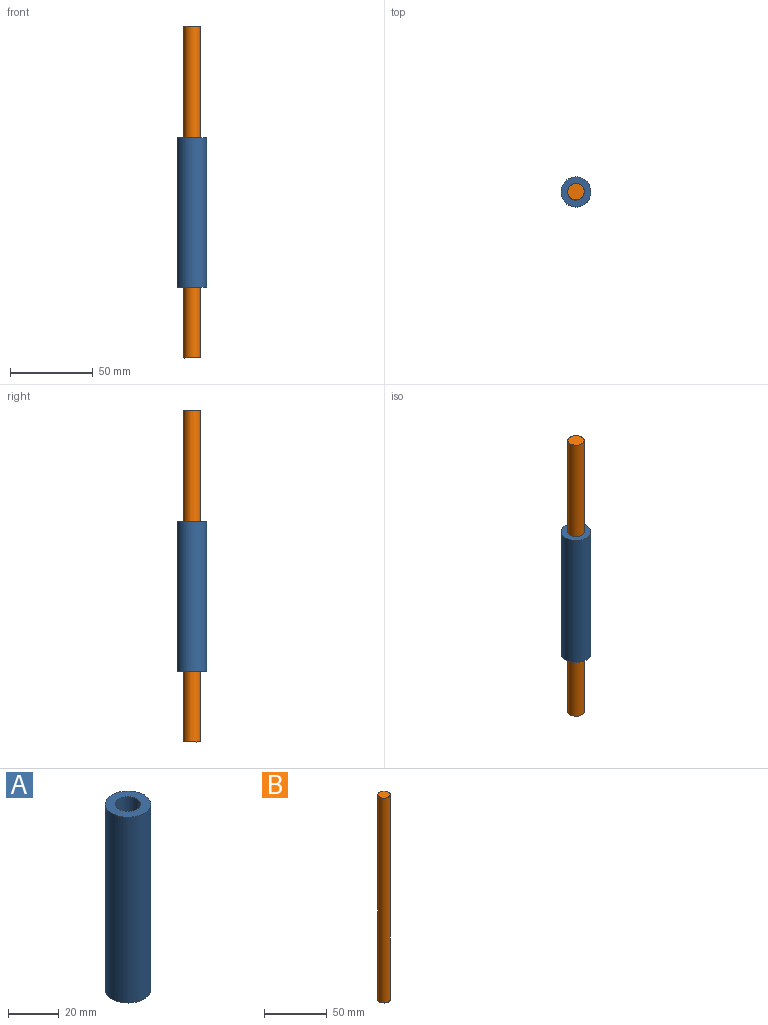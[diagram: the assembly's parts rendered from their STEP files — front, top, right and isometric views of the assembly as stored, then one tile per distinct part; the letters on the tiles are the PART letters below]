
ASSEMBLY  parts=2 mates=1
PART A: 4 faces, bbox 18x18x90 mm
  f0: cylinder r=5mm len=90mm, axis (0,0,-1), area 2827.4mm2, adj f2,f3
  f1: cylinder r=9mm len=90mm, axis (0,0,-1), area 5089.4mm2, adj f2,f3
  f2: plane 18x18mm, normal (0,0,1), area 175.9mm2, adj f0,f1
  f3: plane 18x18mm, normal (0,0,-1), area 175.9mm2, adj f0,f1
PART B: 3 faces, bbox 9.9x9.9x200 mm
  f0: cylinder r=4.95mm len=200mm, axis (0,0,-1), area 6220.4mm2, adj f1,f2
  f1: plane 9.9x9.9mm, normal (0,0,1), area 77mm2, adj f0
  f2: plane 9.9x9.9mm, normal (0,0,-1), area 77mm2, adj f0
PLACE A t=(-40.84,-32.48,-9.94)mm
PLACE B t=(-40.84,-32.48,-142.57)mm
MATE slider A.f0 <-> B.f0  axis (0,0,-1) through (-40.84,-32.48,80.06)mm
